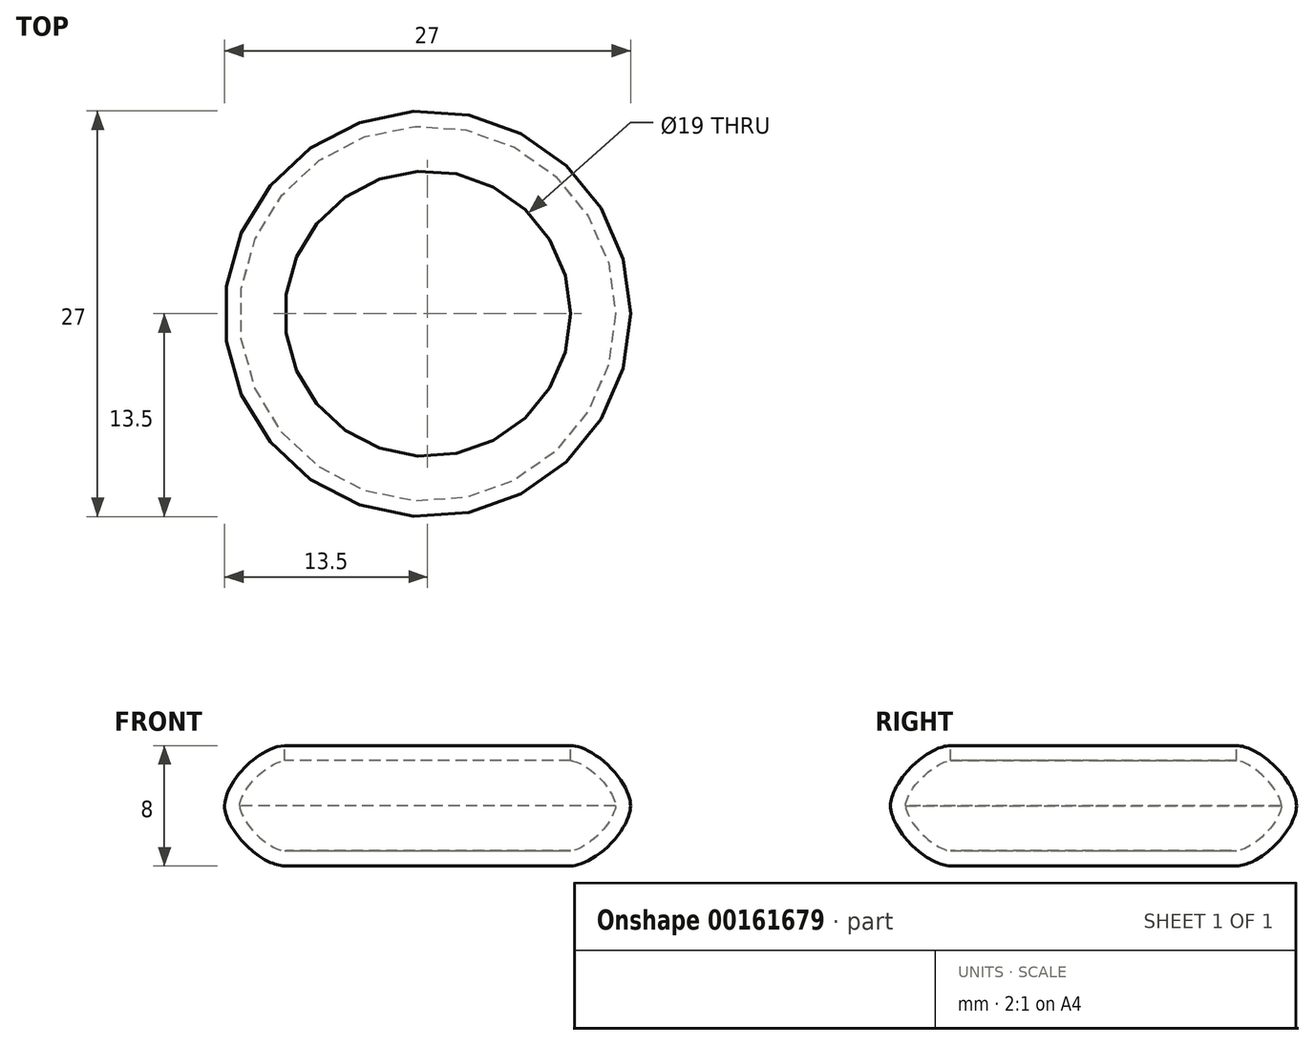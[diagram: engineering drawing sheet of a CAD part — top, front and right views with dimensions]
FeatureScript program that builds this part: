
annotation { "Feature Type Name" : "Feature", "Feature Type Description" : "" }
export const myFeature = defineFeature(function(context is Context, id is Id, definition is map)
    precondition{}
    {
        {
            var Q0;
            Q0=qCreatedBy(makeId("Top.planeOp"),FACE);
            var sketch = newSketch(context, id + "F0", { "sketchPlane" : qUnion([Q0])});
            skCircle(sketch, "E0", {"center": v(0, 0) * mm, "radius": 13.5 * mm});
            skLineSegment(sketch, "E1", {"start": v(-12.07, 6.04) * mm, "end": v(12.07, -6.04) * mm, "construction": true});
            skLineSegment(sketch, "E2", {"start": v(12.07, 6.04) * mm, "end": v(-12.07, -6.04) * mm, "construction": true});
            skSolve(sketch);
        }
        {
            var Q0;
            Q0 = qSketchRegion(id + "F0", true);
            extrude(context, id + "F1", {"entities" : qUnion([Q0]), "depth" : 8 * mm});
        }
        {
            var Q0;
            Q0=makeQuery(id+"F1.opExtrude","CAP_FACE",FACE,{"disambiguationData":[OSD([sQuery(id+"F0.wireOp",EDGE,"E0")])],"isStart":false});
            var Q1;
            Q1=makeQuery(id+"F1.opExtrude","CAP_EDGE",EDGE,{"disambiguationData":[OSD([sQuery(id+"F0.wireOp",EDGE,"E0")])],"isStart":true});
            fillet(context, id + "F2", {"entities" : qUnion([Q0, Q1]), "radius" : 4 * mm, "tangentPropagation" : true, "rho" : 0.3, "crossSection" : FilletCrossSection.CONIC, "allowEdgeOverflow" : false});
        }
        {
            var Q0;
            Q0=makeQuery(id+"F1.opExtrude","CAP_FACE",FACE,{"disambiguationData":[OSD([sQuery(id+"F0.wireOp",EDGE,"E0")])],"isStart":false});
            var Q1;
            Q1=makeQuery(id+"F1.opExtrude","SWEPT_BODY",BODY,{"disambiguationData":[OSD([sQuery(id+"F0.wireOp",EDGE,"E0")])]});
            shell(context, id + "F3", {"isHollow" : true, "entities" : qUnion([Q0]), "parts" : qUnion([Q1]), "thickness" : 1 * mm});
        }
        {
            var Q0;
            Q0=makeQuery(id+"F1.opExtrude","CAP_FACE",FACE,{"disambiguationData":[OSD([sQuery(id+"F0.wireOp",EDGE,"E0")])],"isStart":false});
            var sketch = newSketch(context, id + "F4", { "sketchPlane" : qUnion([Q0])});
            skLineSegment(sketch, "E3", {"start": v(0, 0) * mm, "end": v(8.3, 4.6) * mm, "construction": true});
            skCircle(sketch, "E4", {"center": v(0, 0) * mm, "radius": 9.5 * mm});
            skSolve(sketch);
        }
        {
            var Q0;
            Q0=makeQuery(id+"F4.imprint","IMPRINT",FACE,{"disambiguationData":[TD([[makeQuery(id+"F4.imprint","IMPRINT",EDGE,{"derivedFrom":sQuery(id+"F4.wireOp",EDGE,"E4")}),1.0]])]});
            var Q1;
            Q1=sQuery(id+"F4.wireOp",EDGE,"E4");
            extrude(context, id + "F5", {"entities" : qUnion([Q0]), "operationType" : NewBodyOperationType.REMOVE, "surfaceEntities" : qUnion([Q1]), "oppositeDirection" : true, "depth" : 1 * mm});
        }
    });
